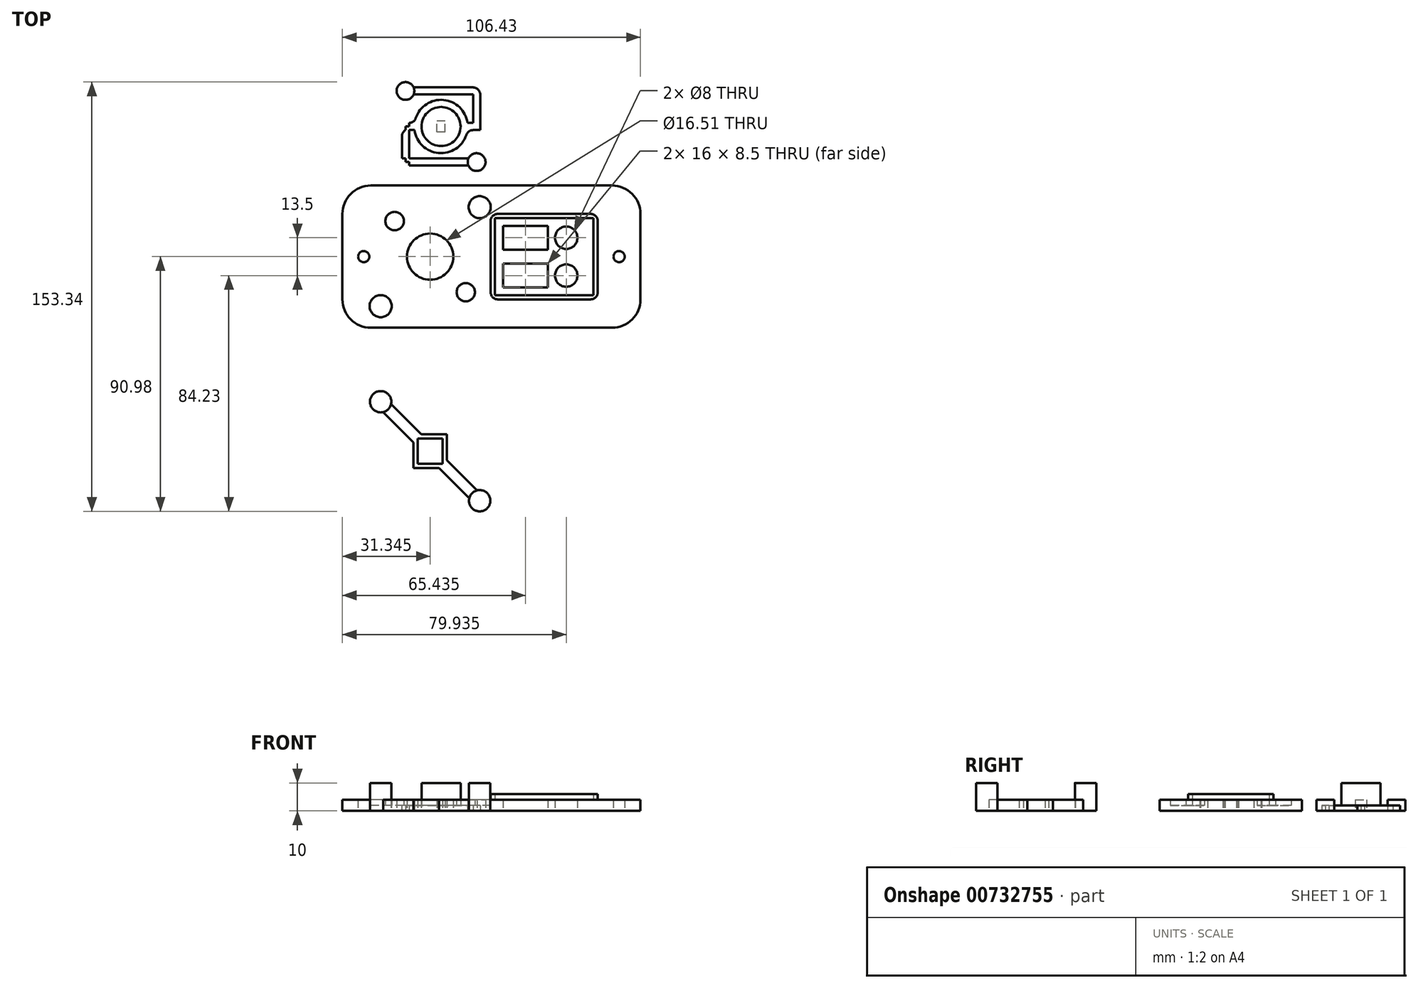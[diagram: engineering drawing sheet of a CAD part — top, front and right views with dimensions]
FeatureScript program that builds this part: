
annotation { "Feature Type Name" : "Feature", "Feature Type Description" : "" }
export const myFeature = defineFeature(function(context is Context, id is Id, definition is map)
    precondition{}
    {
        {
            var Q0;
            Q0=qCreatedBy(makeId("Top.planeOp"),FACE);
            var sketch = newSketch(context, id + "F0", { "sketchPlane" : qUnion([Q0])});
            skLineSegment(sketch, "E0.bottom", {"start": v(49.6, -25.4) * mm, "end": v(-56.82, -25.4) * mm});
            skLineSegment(sketch, "E0.top", {"start": v(49.6, 25.4) * mm, "end": v(-56.82, 25.4) * mm});
            skLineSegment(sketch, "E0.left", {"start": v(49.6, -25.4) * mm, "end": v(49.6, 25.4) * mm});
            skLineSegment(sketch, "E0.right", {"start": v(-56.82, -25.4) * mm, "end": v(-56.82, 25.4) * mm});
            skCircle(sketch, "E1", {"center": v(-49.2, 0) * mm, "radius": 2 * mm});
            skCircle(sketch, "E2", {"center": v(41.98, 0) * mm, "radius": 2 * mm});
            skPoint(sketch, "E3.middle", {"position": v(0, 0) * mm});
            skLineSegment(sketch, "E4.bottom", {"start": v(32.86, -13.75) * mm, "end": v(-2.39, -13.75) * mm});
            skLineSegment(sketch, "E4.top", {"start": v(32.86, 13.75) * mm, "end": v(-2.39, 13.75) * mm});
            skLineSegment(sketch, "E4.left", {"start": v(32.86, -13.75) * mm, "end": v(32.86, 13.75) * mm});
            skLineSegment(sketch, "E4.right", {"start": v(-2.39, -13.75) * mm, "end": v(-2.39, 13.75) * mm});
            skPoint(sketch, "E4.middle", {"position": v(15.24, 0) * mm});
            skLineSegment(sketch, "E5.bottom", {"start": v(34.36, -15.25) * mm, "end": v(-3.89, -15.25) * mm});
            skLineSegment(sketch, "E5.top", {"start": v(34.37, 15.25) * mm, "end": v(-3.89, 15.25) * mm});
            skLineSegment(sketch, "E5.left", {"start": v(34.37, -15.25) * mm, "end": v(34.37, 15.25) * mm});
            skLineSegment(sketch, "E5.right", {"start": v(-3.89, -15.25) * mm, "end": v(-3.88, 15.25) * mm});
            skCircle(sketch, "E6", {"center": v(23.11, 6.75) * mm, "radius": 4 * mm});
            skCircle(sketch, "E7", {"center": v(23.11, -6.75) * mm, "radius": 4 * mm});
            skLineSegment(sketch, "E8.bottom", {"start": v(16.61, 2.5) * mm, "end": v(0.62, 2.5) * mm});
            skLineSegment(sketch, "E8.top", {"start": v(16.61, 11) * mm, "end": v(0.61, 11) * mm});
            skLineSegment(sketch, "E8.left", {"start": v(16.61, 2.5) * mm, "end": v(16.61, 11) * mm});
            skLineSegment(sketch, "E8.right", {"start": v(0.61, 2.5) * mm, "end": v(0.61, 11) * mm});
            skPoint(sketch, "E8.middle", {"position": v(8.61, 6.75) * mm});
            skPoint(sketch, "E9.middle.positionSnap0", {"position": v(8.62, 2.5) * mm});
            skPoint(sketch, "E9.centerSnap0", {"position": v(8.62, 2.5) * mm});
            skLineSegment(sketch, "E10.bottom", {"start": v(16.62, -11) * mm, "end": v(0.61, -11) * mm});
            skLineSegment(sketch, "E10.top", {"start": v(16.62, -2.5) * mm, "end": v(0.61, -2.5) * mm});
            skLineSegment(sketch, "E10.left", {"start": v(16.62, -11) * mm, "end": v(16.62, -2.5) * mm});
            skLineSegment(sketch, "E10.right", {"start": v(0.61, -11) * mm, "end": v(0.61, -2.5) * mm});
            skPoint(sketch, "E10.middle", {"position": v(8.62, -6.75) * mm});
            skCircle(sketch, "E11", {"center": v(-25.48, 0) * mm, "radius": 8.26 * mm});
            skPoint(sketch, "E12", {"position": v(-38.03, 0) * mm});
            skCircle(sketch, "E13", {"center": v(-38.18, 12.7) * mm, "radius": 3.3 * mm});
            skCircle(sketch, "E14", {"center": v(-12.78, -12.7) * mm, "radius": 3.26 * mm});
            skCircle(sketch, "E15", {"center": v(-7.8, 17.68) * mm, "radius": 3.94 * mm});
            skCircle(sketch, "E16", {"center": v(-43.15, -17.68) * mm, "radius": 3.94 * mm});
            skSolve(sketch);
        }
        {
            var Q0;
            Q0=makeQuery(id+"F0.imprint","IMPRINT",FACE,{"disambiguationData":[TD([[makeQuery(id+"F0.imprint","IMPRINT",EDGE,{"derivedFrom":sQuery(id+"F0.wireOp",EDGE,"E0.bottom")}),-1.0]])]});
            var Q1;
            {var subQ0=sQuery(id+"F0.wireOp",EDGE,"NFAVwWTG-spcd-rime-vcjI-FE1p5MGocjtY.bottom");Q1=makeQuery(id+"F0.imprint","IMPRINT",FACE,{"disambiguationData":[TD([[makeQuery(id+"F0.imprint","IMPRINT",EDGE,{"derivedFrom":subQ0}),-1.0]])]});}
            var Q2;
            {var subQ5=sQuery(id+"F0.wireOp",EDGE,"ZG334M0x-5Rls-wxhw-2hUb-fdzan72Nvhxe.top");Q2=makeQuery(id+"F0.imprint","IMPRINT",FACE,{"disambiguationData":[TD([[makeQuery(id+"F0.imprint","IMPRINT",EDGE,{"derivedFrom":subQ5}),-1.0]])]});}
            var Q3;
            {var subQ0=sQuery(id+"F0.wireOp",EDGE,"ZG334M0x-5Rls-wxhw-2hUb-fdzan72Nvhxe.left");var subQ1=sQuery(id+"F0.wireOp",EDGE,"NFAVwWTG-spcd-rime-vcjI-FE1p5MGocjtY.top");var subQ2=makeQuery(id+"F0.imprint","INTERSECT",VERTEX,{"derivedFrom":[subQ1,subQ0]});Q3=makeQuery(id+"F0.imprint","IMPRINT",FACE,{"disambiguationData":[TD([[makeQuery(id+"F0.imprint","IMPRINT",EDGE,{"disambiguationData":[TD([[subQ2,-1.0]])],"derivedFrom":subQ1}),-1.0]])]});}
            var Q4;
            Q4=makeQuery(id+"F0.imprint","IMPRINT",FACE,{"disambiguationData":[TD([[makeQuery(id+"F0.imprint","IMPRINT",EDGE,{"derivedFrom":sQuery(id+"F0.wireOp",EDGE,"HurXRLFW-uDG5-7jJ5-xfbs-HCGxW7BJ1Di5.bottom")}),1.0]])]});
            var Q5;
            {var subQ0=sQuery(id+"F0.wireOp",EDGE,"kk5diSvV-CPj0-MubV-pmVb-ffXCNmJJ0Jb6.bottom");var subQ1=sQuery(id+"F0.wireOp",EDGE,"gLoKTOQZ-337w-JPuW-fgbR-GKVzhC9TP4NV.right");var subQ2=makeQuery(id+"F0.imprint","INTERSECT",VERTEX,{"derivedFrom":[subQ1,subQ0]});Q5=makeQuery(id+"F0.imprint","IMPRINT",FACE,{"disambiguationData":[TD([[makeQuery(id+"F0.imprint","IMPRINT",EDGE,{"disambiguationData":[TD([[subQ2,1.0]])],"derivedFrom":subQ1}),-1.0]])]});}
            var Q6;
            {var subQ5=sQuery(id+"F0.wireOp",EDGE,"ZG334M0x-5Rls-wxhw-2hUb-fdzan72Nvhxe.bottom");Q6=makeQuery(id+"F0.imprint","IMPRINT",FACE,{"disambiguationData":[TD([[makeQuery(id+"F0.imprint","IMPRINT",EDGE,{"derivedFrom":subQ5}),1.0]])]});}
            var Q7;
            {var subQ0=sQuery(id+"F0.wireOp",EDGE,"gLoKTOQZ-337w-JPuW-fgbR-GKVzhC9TP4NV.left");var subQ1=sQuery(id+"F0.wireOp",EDGE,"NFAVwWTG-spcd-rime-vcjI-FE1p5MGocjtY.top");var subQ2=makeQuery(id+"F0.imprint","INTERSECT",VERTEX,{"derivedFrom":[subQ1,subQ0]});Q7=makeQuery(id+"F0.imprint","IMPRINT",FACE,{"disambiguationData":[TD([[makeQuery(id+"F0.imprint","IMPRINT",EDGE,{"disambiguationData":[TD([[subQ2,1.0]])],"derivedFrom":subQ1}),-1.0]])]});}
            var Q8;
            {var subQ5=sQuery(id+"F0.wireOp",EDGE,"kk5diSvV-CPj0-MubV-pmVb-ffXCNmJJ0Jb6.left");Q8=makeQuery(id+"F0.imprint","IMPRINT",FACE,{"disambiguationData":[TD([[makeQuery(id+"F0.imprint","IMPRINT",EDGE,{"derivedFrom":subQ5}),1.0]])]});}
            var Q9;
            {var subQ5=sQuery(id+"F0.wireOp",EDGE,"gLoKTOQZ-337w-JPuW-fgbR-GKVzhC9TP4NV.bottom");Q9=makeQuery(id+"F0.imprint","IMPRINT",FACE,{"disambiguationData":[TD([[makeQuery(id+"F0.imprint","IMPRINT",EDGE,{"derivedFrom":subQ5}),1.0]])]});}
            var Q10;
            Q10=makeQuery(id+"F0.imprint","IMPRINT",FACE,{"disambiguationData":[TD([[makeQuery(id+"F0.imprint","IMPRINT",EDGE,{"derivedFrom":sQuery(id+"F0.wireOp",EDGE,"E3.bottom")}),-1.0]])]});
            var Q11;
            Q11=makeQuery(id+"F0.imprint","IMPRINT",FACE,{"disambiguationData":[TD([[makeQuery(id+"F0.imprint","IMPRINT",EDGE,{"derivedFrom":sQuery(id+"F0.wireOp",EDGE,"E4.bottom")}),1.0]])]});
            var Q12;
            Q12=makeQuery(id+"F0.imprint","IMPRINT",FACE,{"disambiguationData":[TD([[makeQuery(id+"F0.imprint","IMPRINT",EDGE,{"derivedFrom":sQuery(id+"F0.wireOp",EDGE,"E4.bottom")}),-1.0]])]});
            var Q13;
            Q13=makeQuery(id+"F0.imprint","IMPRINT",FACE,{"disambiguationData":[TD([[makeQuery(id+"F0.imprint","IMPRINT",EDGE,{"derivedFrom":sQuery(id+"F0.wireOp",EDGE,"LiykjJPZ-iI25-web5-QGAd-EsjsID3rz56N.bottom")}),-1.0]])]});
            var Q14;
            Q14=makeQuery(id+"F0.imprint","IMPRINT",FACE,{"disambiguationData":[TD([[makeQuery(id+"F0.imprint","IMPRINT",EDGE,{"derivedFrom":sQuery(id+"F0.wireOp",EDGE,"E13")}),1.0]])]});
            var Q15;
            Q15=makeQuery(id+"F0.imprint","IMPRINT",FACE,{"disambiguationData":[TD([[makeQuery(id+"F0.imprint","IMPRINT",EDGE,{"derivedFrom":sQuery(id+"F0.wireOp",EDGE,"E14")}),1.0]])]});
            var Q16;
            Q16=makeQuery(id+"F0.imprint","IMPRINT",FACE,{"disambiguationData":[TD([[makeQuery(id+"F0.imprint","IMPRINT",EDGE,{"derivedFrom":sQuery(id+"F0.wireOp",EDGE,"E15")}),1.0]])]});
            var Q17;
            Q17=makeQuery(id+"F0.imprint","IMPRINT",FACE,{"disambiguationData":[TD([[makeQuery(id+"F0.imprint","IMPRINT",EDGE,{"derivedFrom":sQuery(id+"F0.wireOp",EDGE,"E16")}),1.0]])]});
            extrude(context, id + "F1", {"entities" : qUnion([Q0, Q1, Q2, Q3, Q4, Q5, Q6, Q7, Q8, Q9, Q10, Q11, Q12, Q13, Q14, Q15, Q16, Q17]), "depth" : 4 * mm, "offsetDistance" : 25.4 * mm});
        }
        {
            var Q0;
            Q0=makeQuery(id+"F1.opExtrude","SWEPT_EDGE",EDGE,{"disambiguationData":[OSD([sQuery(id+"F0.wireOp",EDGE,"E0.bottom"),sQuery(id+"F0.wireOp",EDGE,"E0.right")])]});
            var Q1;
            Q1=makeQuery(id+"F1.opExtrude","SWEPT_EDGE",EDGE,{"disambiguationData":[OSD([sQuery(id+"F0.wireOp",EDGE,"E0.top"),sQuery(id+"F0.wireOp",EDGE,"E0.right")])]});
            var Q2;
            Q2=makeQuery(id+"F1.opExtrude","SWEPT_EDGE",EDGE,{"disambiguationData":[OSD([sQuery(id+"F0.wireOp",EDGE,"E0.top"),sQuery(id+"F0.wireOp",EDGE,"E0.left")])]});
            var Q3;
            Q3=makeQuery(id+"F1.opExtrude","SWEPT_EDGE",EDGE,{"disambiguationData":[OSD([sQuery(id+"F0.wireOp",EDGE,"E0.bottom"),sQuery(id+"F0.wireOp",EDGE,"E0.left")])]});
            fillet(context, id + "F2", {"entities" : qUnion([Q0, Q1, Q2, Q3]), "radius" : 10.16 * mm, "tangentPropagation" : true, "allowEdgeOverflow" : false});
        }
        {
            var Q0;
            Q0=makeQuery(id+"F0.imprint","IMPRINT",FACE,{"disambiguationData":[TD([[makeQuery(id+"F0.imprint","IMPRINT",EDGE,{"derivedFrom":sQuery(id+"F0.wireOp",EDGE,"E4.bottom")}),1.0]])]});
            var Q1;
            Q1=makeQuery(id+"F0.imprint","IMPRINT",FACE,{"disambiguationData":[TD([[makeQuery(id+"F0.imprint","IMPRINT",EDGE,{"derivedFrom":sQuery(id+"F0.wireOp",EDGE,"HurXRLFW-uDG5-7jJ5-xfbs-HCGxW7BJ1Di5.bottom")}),1.0]])]});
            extrude(context, id + "F3", {"entities" : qUnion([Q0, Q1]), "operationType" : NewBodyOperationType.ADD, "depth" : 6 * mm, "offsetDistance" : 25.4 * mm});
        }
        {
            var Q0;
            Q0=qCreatedBy(makeId("Top.planeOp"),FACE);
            var sketch = newSketch(context, id + "F4", { "sketchPlane" : qUnion([Q0])});
            skCircle(sketch, "E17", {"center": v(-21.59, 46.48) * mm, "radius": 9.53 * mm});
            skCircle(sketch, "E18", {"center": v(-34.29, 59.18) * mm, "radius": 3.18 * mm});
            skCircle(sketch, "E19", {"center": v(-8.89, 33.78) * mm, "radius": 3.18 * mm});
            skLineSegment(sketch, "E20", {"start": v(-34.29, 59.18) * mm, "end": v(-8.89, 59.18) * mm});
            skLineSegment(sketch, "E21", {"start": v(-8.89, 59.18) * mm, "end": v(-8.89, 46.48) * mm});
            skLineSegment(sketch, "E22", {"start": v(-8.89, 46.48) * mm, "end": v(-12.06, 46.48) * mm});
            skLineSegment(sketch, "E23.bottom", {"start": v(-8.89, 60.45) * mm, "end": v(-34.29, 60.45) * mm});
            skLineSegment(sketch, "E23.top", {"start": v(-8.89, 57.91) * mm, "end": v(-34.29, 57.91) * mm});
            skLineSegment(sketch, "E23.left", {"start": v(-8.89, 60.45) * mm, "end": v(-8.89, 57.91) * mm});
            skLineSegment(sketch, "E23.right", {"start": v(-34.29, 60.45) * mm, "end": v(-34.29, 57.91) * mm});
            skPoint(sketch, "E23.middle", {"position": v(-21.59, 59.18) * mm});
            skLineSegment(sketch, "E24.bottom", {"start": v(-7.62, 45.21) * mm, "end": v(-10.16, 45.21) * mm});
            skLineSegment(sketch, "E24.top", {"start": v(-7.62, 60.45) * mm, "end": v(-10.16, 60.45) * mm});
            skLineSegment(sketch, "E24.left", {"start": v(-7.62, 45.21) * mm, "end": v(-7.62, 60.45) * mm});
            skLineSegment(sketch, "E24.right", {"start": v(-10.16, 45.21) * mm, "end": v(-10.16, 60.45) * mm});
            skPoint(sketch, "E24.middle", {"position": v(-8.89, 52.83) * mm});
            skLineSegment(sketch, "E25.bottom", {"start": v(-7.62, 45.21) * mm, "end": v(-13.33, 45.21) * mm});
            skLineSegment(sketch, "E25.top", {"start": v(-7.62, 47.75) * mm, "end": v(-13.33, 47.75) * mm});
            skLineSegment(sketch, "E25.left", {"start": v(-7.62, 45.21) * mm, "end": v(-7.62, 47.75) * mm});
            skLineSegment(sketch, "E25.right", {"start": v(-13.33, 45.21) * mm, "end": v(-13.33, 47.75) * mm});
            skPoint(sketch, "E25.middle", {"position": v(-10.48, 46.48) * mm});
            skLineSegment(sketch, "E26", {"start": v(-31.11, 46.48) * mm, "end": v(-34.29, 46.48) * mm});
            skLineSegment(sketch, "E27", {"start": v(-34.29, 46.48) * mm, "end": v(-34.29, 33.78) * mm});
            skLineSegment(sketch, "E28", {"start": v(-34.29, 33.78) * mm, "end": v(-8.89, 33.78) * mm});
            skLineSegment(sketch, "E29.bottom", {"start": v(-7.62, 35.05) * mm, "end": v(-35.56, 35.05) * mm});
            skLineSegment(sketch, "E29.top", {"start": v(-7.62, 32.51) * mm, "end": v(-35.56, 32.51) * mm});
            skLineSegment(sketch, "E29.left", {"start": v(-7.62, 35.05) * mm, "end": v(-7.62, 32.51) * mm});
            skLineSegment(sketch, "E29.right", {"start": v(-35.56, 35.05) * mm, "end": v(-35.56, 32.51) * mm});
            skPoint(sketch, "E29.middle", {"position": v(-21.59, 33.78) * mm});
            skLineSegment(sketch, "E30.bottom", {"start": v(-35.56, 32.51) * mm, "end": v(-33.02, 32.51) * mm});
            skLineSegment(sketch, "E30.top", {"start": v(-35.56, 47.75) * mm, "end": v(-33.02, 47.75) * mm});
            skLineSegment(sketch, "E30.left", {"start": v(-35.56, 32.51) * mm, "end": v(-35.56, 47.75) * mm});
            skLineSegment(sketch, "E30.right", {"start": v(-33.02, 32.51) * mm, "end": v(-33.02, 47.75) * mm});
            skPoint(sketch, "E30.middle", {"position": v(-34.29, 40.13) * mm});
            skLineSegment(sketch, "E31.bottom", {"start": v(-35.56, 47.75) * mm, "end": v(-29.84, 47.75) * mm});
            skLineSegment(sketch, "E31.top", {"start": v(-35.56, 45.21) * mm, "end": v(-29.84, 45.21) * mm});
            skLineSegment(sketch, "E31.left", {"start": v(-35.56, 47.75) * mm, "end": v(-35.56, 45.21) * mm});
            skLineSegment(sketch, "E31.right", {"start": v(-29.84, 47.75) * mm, "end": v(-29.84, 45.21) * mm});
            skPoint(sketch, "E31.middle", {"position": v(-32.7, 46.48) * mm});
            skCircle(sketch, "E32", {"center": v(-21.59, 46.48) * mm, "radius": 6.99 * mm});
            skLineSegment(sketch, "E33.bottom", {"start": v(-20.09, 44.48) * mm, "end": v(-23.09, 44.48) * mm});
            skLineSegment(sketch, "E33.top", {"start": v(-20.09, 48.48) * mm, "end": v(-23.09, 48.48) * mm});
            skLineSegment(sketch, "E33.left", {"start": v(-20.09, 44.48) * mm, "end": v(-20.09, 48.48) * mm});
            skLineSegment(sketch, "E33.right", {"start": v(-23.09, 44.48) * mm, "end": v(-23.09, 48.48) * mm});
            skSolve(sketch);
        }
        {
            var Q0;
            {var subQ0=sQuery(id+"F4.wireOp",EDGE,"E25.right");Q0=makeQuery(id+"F4.imprint","IMPRINT",FACE,{"disambiguationData":[TD([[makeQuery(id+"F4.imprint","IMPRINT",EDGE,{"derivedFrom":subQ0}),1.0]])]});}
            var Q1;
            {var subQ5=sQuery(id+"F4.wireOp",EDGE,"E29.left");Q1=makeQuery(id+"F4.imprint","IMPRINT",FACE,{"disambiguationData":[TD([[makeQuery(id+"F4.imprint","IMPRINT",EDGE,{"derivedFrom":subQ5}),1.0]])]});}
            var Q2;
            {var subQ2=sQuery(id+"F4.wireOp",EDGE,"E23.bottom");var subQ6=sQuery(id+"F4.wireOp",EDGE,"E18");var subQ8=makeQuery(id+"F4.imprint","INTERSECT",VERTEX,{"derivedFrom":[subQ6,subQ2]});Q2=makeQuery(id+"F4.imprint","IMPRINT",FACE,{"disambiguationData":[TD([[makeQuery(id+"F4.imprint","IMPRINT",EDGE,{"disambiguationData":[TD([[subQ8,-1.0]])],"derivedFrom":subQ6}),1.0]])]});}
            var Q3;
            {var subQ0=sQuery(id+"F4.wireOp",EDGE,"E23.bottom");var subQ1=sQuery(id+"F4.wireOp",EDGE,"E18");var subQ2=makeQuery(id+"F4.imprint","INTERSECT",VERTEX,{"derivedFrom":[subQ1,subQ0]});Q3=makeQuery(id+"F4.imprint","IMPRINT",FACE,{"disambiguationData":[TD([[makeQuery(id+"F4.imprint","IMPRINT",EDGE,{"disambiguationData":[TD([[subQ2,1.0]])],"derivedFrom":subQ1}),1.0]])]});}
            var Q4;
            {var subQ0=sQuery(id+"F4.wireOp",EDGE,"E23.top");var subQ1=sQuery(id+"F4.wireOp",EDGE,"E18");var subQ2=makeQuery(id+"F4.imprint","INTERSECT",VERTEX,{"derivedFrom":[subQ1,subQ0]});Q4=makeQuery(id+"F4.imprint","IMPRINT",FACE,{"disambiguationData":[TD([[makeQuery(id+"F4.imprint","IMPRINT",EDGE,{"disambiguationData":[TD([[subQ2,-1.0]])],"derivedFrom":subQ1}),1.0]])]});}
            var Q5;
            {var subQ0=sQuery(id+"F4.wireOp",EDGE,"E23.top");var subQ1=sQuery(id+"F4.wireOp",EDGE,"E18");var subQ2=makeQuery(id+"F4.imprint","INTERSECT",VERTEX,{"derivedFrom":[subQ1,subQ0]});Q5=makeQuery(id+"F4.imprint","IMPRINT",FACE,{"disambiguationData":[TD([[makeQuery(id+"F4.imprint","IMPRINT",EDGE,{"disambiguationData":[TD([[subQ2,-1.0]])],"derivedFrom":subQ1}),-1.0]])]});}
            var Q6;
            {var subQ0=sQuery(id+"F4.wireOp",EDGE,"E23.bottom");var subQ1=sQuery(id+"F4.wireOp",EDGE,"E18");var subQ2=makeQuery(id+"F4.imprint","INTERSECT",VERTEX,{"derivedFrom":[subQ1,subQ0]});Q6=makeQuery(id+"F4.imprint","IMPRINT",FACE,{"disambiguationData":[TD([[makeQuery(id+"F4.imprint","IMPRINT",EDGE,{"disambiguationData":[TD([[subQ2,1.0]])],"derivedFrom":subQ1}),-1.0]])]});}
            var Q7;
            {var subQ3=sQuery(id+"F4.wireOp",EDGE,"E24.left");Q7=makeQuery(id+"F4.imprint","IMPRINT",FACE,{"disambiguationData":[TD([[makeQuery(id+"F4.imprint","IMPRINT",EDGE,{"derivedFrom":subQ3}),1.0]])]});}
            var Q8;
            {var subQ0=sQuery(id+"F4.wireOp",EDGE,"E23.top");var subQ5=sQuery(id+"F4.wireOp",EDGE,"E24.right");var subQ7=makeQuery(id+"F4.imprint","INTERSECT",VERTEX,{"derivedFrom":[subQ0,subQ5]});Q8=makeQuery(id+"F4.imprint","IMPRINT",FACE,{"disambiguationData":[TD([[makeQuery(id+"F4.imprint","IMPRINT",EDGE,{"disambiguationData":[TD([[subQ7,1.0]])],"derivedFrom":subQ5}),-1.0]])]});}
            var Q9;
            {var subQ0=sQuery(id+"F4.wireOp",EDGE,"E23.left");var subQ1=sQuery(id+"F4.wireOp",EDGE,"E20");var subQ2=makeQuery(id+"F4.imprint","INTERSECT",VERTEX,{"derivedFrom":[subQ1,subQ0]});Q9=makeQuery(id+"F4.imprint","IMPRINT",FACE,{"disambiguationData":[TD([[makeQuery(id+"F4.imprint","IMPRINT",EDGE,{"disambiguationData":[TD([[subQ2,1.0]])],"derivedFrom":subQ1}),-1.0]])]});}
            var Q10;
            {var subQ0=sQuery(id+"F4.wireOp",EDGE,"E23.left");var subQ1=sQuery(id+"F4.wireOp",EDGE,"E20");var subQ2=makeQuery(id+"F4.imprint","INTERSECT",VERTEX,{"derivedFrom":[subQ1,subQ0]});Q10=makeQuery(id+"F4.imprint","IMPRINT",FACE,{"disambiguationData":[TD([[makeQuery(id+"F4.imprint","IMPRINT",EDGE,{"disambiguationData":[TD([[subQ2,1.0]])],"derivedFrom":subQ1}),1.0]])]});}
            var Q11;
            {var subQ5=sQuery(id+"F4.wireOp",EDGE,"E25.left");Q11=makeQuery(id+"F4.imprint","IMPRINT",FACE,{"disambiguationData":[TD([[makeQuery(id+"F4.imprint","IMPRINT",EDGE,{"derivedFrom":subQ5}),1.0]])]});}
            var Q12;
            {var subQ0=sQuery(id+"F4.wireOp",EDGE,"E22");var subQ1=sQuery(id+"F4.wireOp",EDGE,"E21");var subQ2=makeQuery(id+"F4.imprint","INTERSECT",VERTEX,{"derivedFrom":[subQ1,subQ0]});Q12=makeQuery(id+"F4.imprint","IMPRINT",FACE,{"disambiguationData":[TD([[makeQuery(id+"F4.imprint","IMPRINT",EDGE,{"disambiguationData":[TD([[subQ2,1.0]])],"derivedFrom":subQ1}),-1.0]])]});}
            var Q13;
            {var subQ0=sQuery(id+"F4.wireOp",EDGE,"E22");var subQ1=sQuery(id+"F4.wireOp",EDGE,"E17");var subQ2=makeQuery(id+"F4.imprint","INTERSECT",VERTEX,{"derivedFrom":[subQ1,subQ0]});Q13=makeQuery(id+"F4.imprint","IMPRINT",FACE,{"disambiguationData":[TD([[makeQuery(id+"F4.imprint","IMPRINT",EDGE,{"disambiguationData":[TD([[subQ2,-1.0]])],"derivedFrom":subQ1}),-1.0]])]});}
            var Q14;
            {var subQ0=sQuery(id+"F4.wireOp",EDGE,"E22");var subQ1=sQuery(id+"F4.wireOp",EDGE,"E17");var subQ2=makeQuery(id+"F4.imprint","INTERSECT",VERTEX,{"derivedFrom":[subQ1,subQ0]});Q14=makeQuery(id+"F4.imprint","IMPRINT",FACE,{"disambiguationData":[TD([[makeQuery(id+"F4.imprint","IMPRINT",EDGE,{"disambiguationData":[TD([[subQ2,1.0]])],"derivedFrom":subQ1}),-1.0]])]});}
            var Q15;
            {var subQ0=sQuery(id+"F4.wireOp",EDGE,"E25.right");Q15=makeQuery(id+"F4.imprint","IMPRINT",FACE,{"disambiguationData":[TD([[makeQuery(id+"F4.imprint","IMPRINT",EDGE,{"derivedFrom":subQ0}),-1.0]])]});}
            var Q16;
            {var subQ0=sQuery(id+"F4.wireOp",EDGE,"E26");var subQ1=sQuery(id+"F4.wireOp",EDGE,"E17");var subQ2=makeQuery(id+"F4.imprint","INTERSECT",VERTEX,{"derivedFrom":[subQ1,subQ0]});Q16=makeQuery(id+"F4.imprint","IMPRINT",FACE,{"disambiguationData":[TD([[makeQuery(id+"F4.imprint","IMPRINT",EDGE,{"disambiguationData":[TD([[subQ2,1.0]])],"derivedFrom":subQ1}),-1.0]])]});}
            var Q17;
            {var subQ0=sQuery(id+"F4.wireOp",EDGE,"E26");var subQ1=sQuery(id+"F4.wireOp",EDGE,"E17");var subQ2=makeQuery(id+"F4.imprint","INTERSECT",VERTEX,{"derivedFrom":[subQ1,subQ0]});Q17=makeQuery(id+"F4.imprint","IMPRINT",FACE,{"disambiguationData":[TD([[makeQuery(id+"F4.imprint","IMPRINT",EDGE,{"disambiguationData":[TD([[subQ2,-1.0]])],"derivedFrom":subQ1}),-1.0]])]});}
            var Q18;
            {var subQ0=sQuery(id+"F4.wireOp",EDGE,"E31.right");Q18=makeQuery(id+"F4.imprint","IMPRINT",FACE,{"disambiguationData":[TD([[makeQuery(id+"F4.imprint","IMPRINT",EDGE,{"derivedFrom":subQ0}),-1.0]])]});}
            var Q19;
            {var subQ3=sQuery(id+"F4.wireOp",EDGE,"E31.left");Q19=makeQuery(id+"F4.imprint","IMPRINT",FACE,{"disambiguationData":[TD([[makeQuery(id+"F4.imprint","IMPRINT",EDGE,{"derivedFrom":subQ3}),1.0]])]});}
            var Q20;
            {var subQ0=sQuery(id+"F4.wireOp",EDGE,"E27");var subQ1=sQuery(id+"F4.wireOp",EDGE,"E26");var subQ2=makeQuery(id+"F4.imprint","INTERSECT",VERTEX,{"derivedFrom":[subQ1,subQ0]});Q20=makeQuery(id+"F4.imprint","IMPRINT",FACE,{"disambiguationData":[TD([[makeQuery(id+"F4.imprint","IMPRINT",EDGE,{"disambiguationData":[TD([[subQ2,1.0]])],"derivedFrom":subQ1}),1.0]])]});}
            var Q21;
            {var subQ0=sQuery(id+"F4.wireOp",EDGE,"E31.top");var subQ1=sQuery(id+"F4.wireOp",EDGE,"E27");var subQ2=makeQuery(id+"F4.imprint","INTERSECT",VERTEX,{"derivedFrom":[subQ1,subQ0]});Q21=makeQuery(id+"F4.imprint","IMPRINT",FACE,{"disambiguationData":[TD([[makeQuery(id+"F4.imprint","IMPRINT",EDGE,{"disambiguationData":[TD([[subQ2,-1.0]])],"derivedFrom":subQ1}),-1.0]])]});}
            var Q22;
            {var subQ0=sQuery(id+"F4.wireOp",EDGE,"E31.top");var subQ1=sQuery(id+"F4.wireOp",EDGE,"E27");var subQ2=makeQuery(id+"F4.imprint","INTERSECT",VERTEX,{"derivedFrom":[subQ1,subQ0]});Q22=makeQuery(id+"F4.imprint","IMPRINT",FACE,{"disambiguationData":[TD([[makeQuery(id+"F4.imprint","IMPRINT",EDGE,{"disambiguationData":[TD([[subQ2,-1.0]])],"derivedFrom":subQ1}),1.0]])]});}
            var Q23;
            {var subQ9=sQuery(id+"F4.wireOp",EDGE,"E30.bottom");Q23=makeQuery(id+"F4.imprint","IMPRINT",FACE,{"disambiguationData":[TD([[makeQuery(id+"F4.imprint","IMPRINT",EDGE,{"derivedFrom":subQ9}),1.0]])]});}
            var Q24;
            {var subQ0=sQuery(id+"F4.wireOp",EDGE,"E28");var subQ1=sQuery(id+"F4.wireOp",EDGE,"E27");var subQ2=makeQuery(id+"F4.imprint","INTERSECT",VERTEX,{"derivedFrom":[subQ1,subQ0]});Q24=makeQuery(id+"F4.imprint","IMPRINT",FACE,{"disambiguationData":[TD([[makeQuery(id+"F4.imprint","IMPRINT",EDGE,{"disambiguationData":[TD([[subQ2,1.0]])],"derivedFrom":subQ1}),1.0]])]});}
            var Q25;
            {var subQ0=sQuery(id+"F4.wireOp",EDGE,"E28");var subQ1=sQuery(id+"F4.wireOp",EDGE,"E19");var subQ2=makeQuery(id+"F4.imprint","INTERSECT",VERTEX,{"derivedFrom":[subQ1,subQ0]});Q25=makeQuery(id+"F4.imprint","IMPRINT",FACE,{"disambiguationData":[TD([[makeQuery(id+"F4.imprint","IMPRINT",EDGE,{"disambiguationData":[TD([[subQ2,1.0]])],"derivedFrom":subQ1}),-1.0]])]});}
            var Q26;
            {var subQ0=sQuery(id+"F4.wireOp",EDGE,"E28");var subQ1=sQuery(id+"F4.wireOp",EDGE,"E19");var subQ2=makeQuery(id+"F4.imprint","INTERSECT",VERTEX,{"derivedFrom":[subQ1,subQ0]});Q26=makeQuery(id+"F4.imprint","IMPRINT",FACE,{"disambiguationData":[TD([[makeQuery(id+"F4.imprint","IMPRINT",EDGE,{"disambiguationData":[TD([[subQ2,-1.0]])],"derivedFrom":subQ1}),-1.0]])]});}
            var Q27;
            {var subQ0=sQuery(id+"F4.wireOp",EDGE,"E29.left");Q27=makeQuery(id+"F4.imprint","IMPRINT",FACE,{"disambiguationData":[TD([[makeQuery(id+"F4.imprint","IMPRINT",EDGE,{"derivedFrom":subQ0}),-1.0]])]});}
            var Q28;
            Q28=makeQuery(id+"F4.imprint","IMPRINT",FACE,{"disambiguationData":[TD([[makeQuery(id+"F4.imprint","IMPRINT",EDGE,{"derivedFrom":sQuery(id+"F4.wireOp",EDGE,"E32")}),1.0]])]});
            var Q29;
            Q29=makeQuery(id+"F4.imprint","IMPRINT",FACE,{"disambiguationData":[TD([[makeQuery(id+"F4.imprint","IMPRINT",EDGE,{"derivedFrom":sQuery(id+"F4.wireOp",EDGE,"E33.bottom")}),-1.0]])]});
            extrude(context, id + "F5", {"entities" : qUnion([Q0, Q1, Q2, Q3, Q4, Q5, Q6, Q7, Q8, Q9, Q10, Q11, Q12, Q13, Q14, Q15, Q16, Q17, Q18, Q19, Q20, Q21, Q22, Q23, Q24, Q25, Q26, Q27, Q28, Q29]), "depth" : 2 * mm, "offsetDistance" : 25.4 * mm});
        }
        {
            var Q0;
            Q0=makeQuery(id+"F4.imprint","IMPRINT",FACE,{"disambiguationData":[TD([[makeQuery(id+"F4.imprint","IMPRINT",EDGE,{"derivedFrom":sQuery(id+"F4.wireOp",EDGE,"E32")}),1.0]])]});
            var Q1;
            Q1=makeQuery(id+"F4.imprint","IMPRINT",FACE,{"disambiguationData":[TD([[makeQuery(id+"F4.imprint","IMPRINT",EDGE,{"derivedFrom":sQuery(id+"F4.wireOp",EDGE,"E33.bottom")}),-1.0]])]});
            extrude(context, id + "F6", {"entities" : qUnion([Q0, Q1]), "operationType" : NewBodyOperationType.ADD, "depth" : 10 * mm, "offsetDistance" : 25.4 * mm});
        }
        {
            var Q0;
            Q0=makeQuery(id+"F5.opExtrude","SWEPT_EDGE",EDGE,{"disambiguationData":[OSD([sQuery(id+"F4.wireOp",EDGE,"E24.top"),sQuery(id+"F4.wireOp",EDGE,"E24.left")])]});
            var Q1;
            Q1=makeQuery(id+"F5.opExtrude","SWEPT_EDGE",EDGE,{"disambiguationData":[OSD([sQuery(id+"F4.wireOp",EDGE,"E25.bottom"),sQuery(id+"F4.wireOp",EDGE,"E25.left")])]});
            var Q2;
            Q2=makeQuery(id+"F5.opExtrude","SWEPT_EDGE",EDGE,{"disambiguationData":[OSD([sQuery(id+"F4.wireOp",EDGE,"E30.bottom"),sQuery(id+"F4.wireOp",EDGE,"E30.left")])]});
            var Q3;
            Q3=makeQuery(id+"F5.opExtrude","SWEPT_EDGE",EDGE,{"disambiguationData":[OSD([sQuery(id+"F4.wireOp",EDGE,"E31.bottom"),sQuery(id+"F4.wireOp",EDGE,"E31.left")])]});
            fillet(context, id + "F7", {"entities" : qUnion([Q0, Q1, Q2, Q3]), "radius" : 2.54 * mm, "tangentPropagation" : true, "allowEdgeOverflow" : false});
        }
        {
            var Q0;
            Q0=makeQuery(id+"F4.imprint","IMPRINT",FACE,{"disambiguationData":[TD([[makeQuery(id+"F4.imprint","IMPRINT",EDGE,{"derivedFrom":sQuery(id+"F4.wireOp",EDGE,"E33.bottom")}),-1.0]])]});
            extrude(context, id + "F8", {"entities" : qUnion([Q0]), "operationType" : NewBodyOperationType.REMOVE, "depth" : 4 * mm, "offsetDistance" : 25.4 * mm});
        }
        {
            var Q0;
            {var subQ2=sQuery(id+"F4.wireOp",EDGE,"E23.bottom");var subQ6=sQuery(id+"F4.wireOp",EDGE,"E18");var subQ8=makeQuery(id+"F4.imprint","INTERSECT",VERTEX,{"derivedFrom":[subQ6,subQ2]});Q0=makeQuery(id+"F4.imprint","IMPRINT",FACE,{"disambiguationData":[TD([[makeQuery(id+"F4.imprint","IMPRINT",EDGE,{"disambiguationData":[TD([[subQ8,-1.0]])],"derivedFrom":subQ6}),1.0]])]});}
            var Q1;
            {var subQ0=sQuery(id+"F4.wireOp",EDGE,"E23.bottom");var subQ1=sQuery(id+"F4.wireOp",EDGE,"E18");var subQ2=makeQuery(id+"F4.imprint","INTERSECT",VERTEX,{"derivedFrom":[subQ1,subQ0]});Q1=makeQuery(id+"F4.imprint","IMPRINT",FACE,{"disambiguationData":[TD([[makeQuery(id+"F4.imprint","IMPRINT",EDGE,{"disambiguationData":[TD([[subQ2,1.0]])],"derivedFrom":subQ1}),1.0]])]});}
            var Q2;
            {var subQ0=sQuery(id+"F4.wireOp",EDGE,"E23.top");var subQ1=sQuery(id+"F4.wireOp",EDGE,"E18");var subQ2=makeQuery(id+"F4.imprint","INTERSECT",VERTEX,{"derivedFrom":[subQ1,subQ0]});Q2=makeQuery(id+"F4.imprint","IMPRINT",FACE,{"disambiguationData":[TD([[makeQuery(id+"F4.imprint","IMPRINT",EDGE,{"disambiguationData":[TD([[subQ2,-1.0]])],"derivedFrom":subQ1}),1.0]])]});}
            var Q3;
            {var subQ5=sQuery(id+"F4.wireOp",EDGE,"E29.left");Q3=makeQuery(id+"F4.imprint","IMPRINT",FACE,{"disambiguationData":[TD([[makeQuery(id+"F4.imprint","IMPRINT",EDGE,{"derivedFrom":subQ5}),1.0]])]});}
            var Q4;
            {var subQ0=sQuery(id+"F4.wireOp",EDGE,"E29.left");Q4=makeQuery(id+"F4.imprint","IMPRINT",FACE,{"disambiguationData":[TD([[makeQuery(id+"F4.imprint","IMPRINT",EDGE,{"derivedFrom":subQ0}),-1.0]])]});}
            extrude(context, id + "F9", {"entities" : qUnion([Q0, Q1, Q2, Q3, Q4]), "operationType" : NewBodyOperationType.ADD, "depth" : 4 * mm, "offsetDistance" : 25.4 * mm});
        }
        {
            var Q0;
            Q0=makeQuery(id+"F0.imprint","IMPRINT",FACE,{"disambiguationData":[TD([[makeQuery(id+"F0.imprint","IMPRINT",EDGE,{"derivedFrom":sQuery(id+"F0.wireOp",EDGE,"E13")}),1.0]])]});
            var Q1;
            Q1=makeQuery(id+"F0.imprint","IMPRINT",FACE,{"disambiguationData":[TD([[makeQuery(id+"F0.imprint","IMPRINT",EDGE,{"derivedFrom":sQuery(id+"F0.wireOp",EDGE,"E14")}),1.0]])]});
            var Q2;
            Q2=makeQuery(id+"F0.imprint","IMPRINT",FACE,{"disambiguationData":[TD([[makeQuery(id+"F0.imprint","IMPRINT",EDGE,{"derivedFrom":sQuery(id+"F0.wireOp",EDGE,"E15")}),1.0]])]});
            var Q3;
            Q3=makeQuery(id+"F0.imprint","IMPRINT",FACE,{"disambiguationData":[TD([[makeQuery(id+"F0.imprint","IMPRINT",EDGE,{"derivedFrom":sQuery(id+"F0.wireOp",EDGE,"E16")}),1.0]])]});
            extrude(context, id + "F10", {"entities" : qUnion([Q0, Q1, Q2, Q3]), "operationType" : NewBodyOperationType.REMOVE, "depth" : 4 * mm, "offsetDistance" : 25.4 * mm, "hasSecondDirection" : true, "secondDirectionOppositeDirection" : false, "secondDirectionDepth" : 2 * mm});
        }
        {
            var Q0;
            Q0=qCreatedBy(makeId("Top.planeOp"),FACE);
            var sketch = newSketch(context, id + "F11", { "sketchPlane" : qUnion([Q0])});
            skPoint(sketch, "E34.0", {"position": v(-25.48, 0) * mm});
            skLineSegment(sketch, "E35.bottom", {"start": v(-20.97, -74) * mm, "end": v(-29.97, -74) * mm});
            skLineSegment(sketch, "E35.top", {"start": v(-20.97, -65) * mm, "end": v(-29.97, -65) * mm});
            skLineSegment(sketch, "E35.left", {"start": v(-20.97, -74) * mm, "end": v(-20.97, -65) * mm});
            skLineSegment(sketch, "E35.right", {"start": v(-29.97, -74) * mm, "end": v(-29.97, -65) * mm});
            skPoint(sketch, "E35.middle", {"position": v(-25.47, -69.5) * mm});
            skLineSegment(sketch, "E36.bottom", {"start": v(-31.47, -63.5) * mm, "end": v(-19.47, -63.5) * mm});
            skLineSegment(sketch, "E36.top", {"start": v(-31.47, -75.5) * mm, "end": v(-19.47, -75.5) * mm});
            skLineSegment(sketch, "E36.left", {"start": v(-31.47, -63.5) * mm, "end": v(-31.47, -75.5) * mm});
            skLineSegment(sketch, "E36.right", {"start": v(-19.47, -63.5) * mm, "end": v(-19.47, -75.5) * mm});
            skLineSegment(sketch, "E37", {"start": v(-31.47, -63.5) * mm, "end": v(-43.15, -51.83) * mm});
            skLineSegment(sketch, "E38.0", {"start": v(-28.65, -63.5) * mm, "end": v(-40.32, -51.83) * mm});
            skLineSegment(sketch, "E39.0", {"start": v(-31.47, -66.33) * mm, "end": v(-43.15, -54.66) * mm});
            skCircle(sketch, "E40", {"center": v(-43.15, -51.83) * mm, "radius": 3.81 * mm});
            skLineSegment(sketch, "E41", {"start": v(-19.47, -75.5) * mm, "end": v(-7.8, -87.17) * mm});
            skCircle(sketch, "E42", {"center": v(-7.8, -87.17) * mm, "radius": 3.81 * mm});
            skLineSegment(sketch, "E43.0", {"start": v(-22.3, -75.5) * mm, "end": v(-9.21, -88.59) * mm});
            skLineSegment(sketch, "E44.0", {"start": v(-19.47, -72.67) * mm, "end": v(-6.39, -85.76) * mm});
            skSolve(sketch);
        }
        {
            var Q0;
            {var subQ0=sQuery(id+"F11.wireOp",EDGE,"E40");var subQ1=makeQuery(id+"F11.imprint","INTERSECT",VERTEX,{"derivedFrom":[sQuery(id+"F11.wireOp",EDGE,"E39.0"),subQ0]});Q0=makeQuery(id+"F11.imprint","IMPRINT",FACE,{"disambiguationData":[TD([[makeQuery(id+"F11.imprint","IMPRINT",EDGE,{"disambiguationData":[TD([[subQ1,-1.0]])],"derivedFrom":subQ0}),1.0]])]});}
            var Q1;
            {var subQ1=sQuery(id+"F11.wireOp",EDGE,"E36.bottom");var subQ3=sQuery(id+"F11.wireOp",EDGE,"E38.0");var subQ4=makeQuery(id+"F11.imprint","INTERSECT",VERTEX,{"derivedFrom":[subQ1,subQ3]});Q1=makeQuery(id+"F11.imprint","IMPRINT",FACE,{"disambiguationData":[TD([[makeQuery(id+"F11.imprint","IMPRINT",EDGE,{"disambiguationData":[TD([[subQ4,-1.0]])],"derivedFrom":subQ3}),1.0]])]});}
            var Q2;
            {var subQ1=sQuery(id+"F11.wireOp",EDGE,"E36.left");var subQ3=sQuery(id+"F11.wireOp",EDGE,"E39.0");var subQ4=makeQuery(id+"F11.imprint","INTERSECT",VERTEX,{"derivedFrom":[subQ1,subQ3]});Q2=makeQuery(id+"F11.imprint","IMPRINT",FACE,{"disambiguationData":[TD([[makeQuery(id+"F11.imprint","IMPRINT",EDGE,{"disambiguationData":[TD([[subQ4,-1.0]])],"derivedFrom":subQ3}),-1.0]])]});}
            var Q3;
            Q3=makeQuery(id+"F11.imprint","IMPRINT",FACE,{"disambiguationData":[TD([[makeQuery(id+"F11.imprint","IMPRINT",EDGE,{"derivedFrom":sQuery(id+"F11.wireOp",EDGE,"E35.bottom")}),1.0]])]});
            var Q4;
            {var subQ3=sQuery(id+"F11.wireOp",EDGE,"E44.0");var subQ5=sQuery(id+"F11.wireOp",EDGE,"E42");var subQ7=makeQuery(id+"F11.imprint","INTERSECT",VERTEX,{"derivedFrom":[subQ5,subQ3]});Q4=makeQuery(id+"F11.imprint","IMPRINT",FACE,{"disambiguationData":[TD([[makeQuery(id+"F11.imprint","IMPRINT",EDGE,{"disambiguationData":[TD([[subQ7,-1.0]])],"derivedFrom":subQ5}),-1.0]])]});}
            var Q5;
            {var subQ3=sQuery(id+"F11.wireOp",EDGE,"E43.0");var subQ5=sQuery(id+"F11.wireOp",EDGE,"E42");var subQ6=makeQuery(id+"F11.imprint","INTERSECT",VERTEX,{"derivedFrom":[subQ5,subQ3]});Q5=makeQuery(id+"F11.imprint","IMPRINT",FACE,{"disambiguationData":[TD([[makeQuery(id+"F11.imprint","IMPRINT",EDGE,{"disambiguationData":[TD([[subQ6,1.0]])],"derivedFrom":subQ5}),-1.0]])]});}
            var Q6;
            {var subQ0=sQuery(id+"F11.wireOp",EDGE,"E42");var subQ1=makeQuery(id+"F11.imprint","INTERSECT",VERTEX,{"derivedFrom":[subQ0,sQuery(id+"F11.wireOp",EDGE,"E44.0")]});Q6=makeQuery(id+"F11.imprint","IMPRINT",FACE,{"disambiguationData":[TD([[makeQuery(id+"F11.imprint","IMPRINT",EDGE,{"disambiguationData":[TD([[subQ1,-1.0]])],"derivedFrom":subQ0}),1.0]])]});}
            extrude(context, id + "F12", {"entities" : qUnion([Q0, Q1, Q2, Q3, Q4, Q5, Q6]), "depth" : 4 * mm, "offsetDistance" : 25.4 * mm});
        }
        {
            var Q0;
            Q0=makeQuery(id+"F3.opExtrude","SWEPT_EDGE",EDGE,{"disambiguationData":[OSD([sQuery(id+"F0.wireOp",EDGE,"E5.top"),sQuery(id+"F0.wireOp",EDGE,"E5.right")])]});
            var Q1;
            Q1=makeQuery(id+"F3.opExtrude","SWEPT_EDGE",EDGE,{"disambiguationData":[OSD([sQuery(id+"F0.wireOp",EDGE,"E5.top"),sQuery(id+"F0.wireOp",EDGE,"E5.left")])]});
            var Q2;
            Q2=makeQuery(id+"F3.opExtrude","SWEPT_EDGE",EDGE,{"disambiguationData":[OSD([sQuery(id+"F0.wireOp",EDGE,"E5.bottom"),sQuery(id+"F0.wireOp",EDGE,"E5.left")])]});
            var Q3;
            Q3=makeQuery(id+"F3.opExtrude","SWEPT_EDGE",EDGE,{"disambiguationData":[OSD([sQuery(id+"F0.wireOp",EDGE,"E5.bottom"),sQuery(id+"F0.wireOp",EDGE,"E5.right")])]});
            fillet(context, id + "F13", {"entities" : qUnion([Q0, Q1, Q2, Q3]), "radius" : 2.54 * mm, "tangentPropagation" : true, "allowEdgeOverflow" : false});
        }
        {
            var Q0;
            {var subQ0=sQuery(id+"F11.wireOp",EDGE,"E40");var subQ1=makeQuery(id+"F11.imprint","INTERSECT",VERTEX,{"derivedFrom":[sQuery(id+"F11.wireOp",EDGE,"E39.0"),subQ0]});Q0=makeQuery(id+"F11.imprint","IMPRINT",FACE,{"disambiguationData":[TD([[makeQuery(id+"F11.imprint","IMPRINT",EDGE,{"disambiguationData":[TD([[subQ1,-1.0]])],"derivedFrom":subQ0}),1.0]])]});}
            var Q1;
            {var subQ0=sQuery(id+"F11.wireOp",EDGE,"E42");var subQ1=makeQuery(id+"F11.imprint","INTERSECT",VERTEX,{"derivedFrom":[subQ0,sQuery(id+"F11.wireOp",EDGE,"E44.0")]});Q1=makeQuery(id+"F11.imprint","IMPRINT",FACE,{"disambiguationData":[TD([[makeQuery(id+"F11.imprint","IMPRINT",EDGE,{"disambiguationData":[TD([[subQ1,-1.0]])],"derivedFrom":subQ0}),1.0]])]});}
            extrude(context, id + "F14", {"entities" : qUnion([Q0, Q1]), "operationType" : NewBodyOperationType.ADD, "depth" : 10 * mm, "offsetDistance" : 25.4 * mm});
        }
    });
